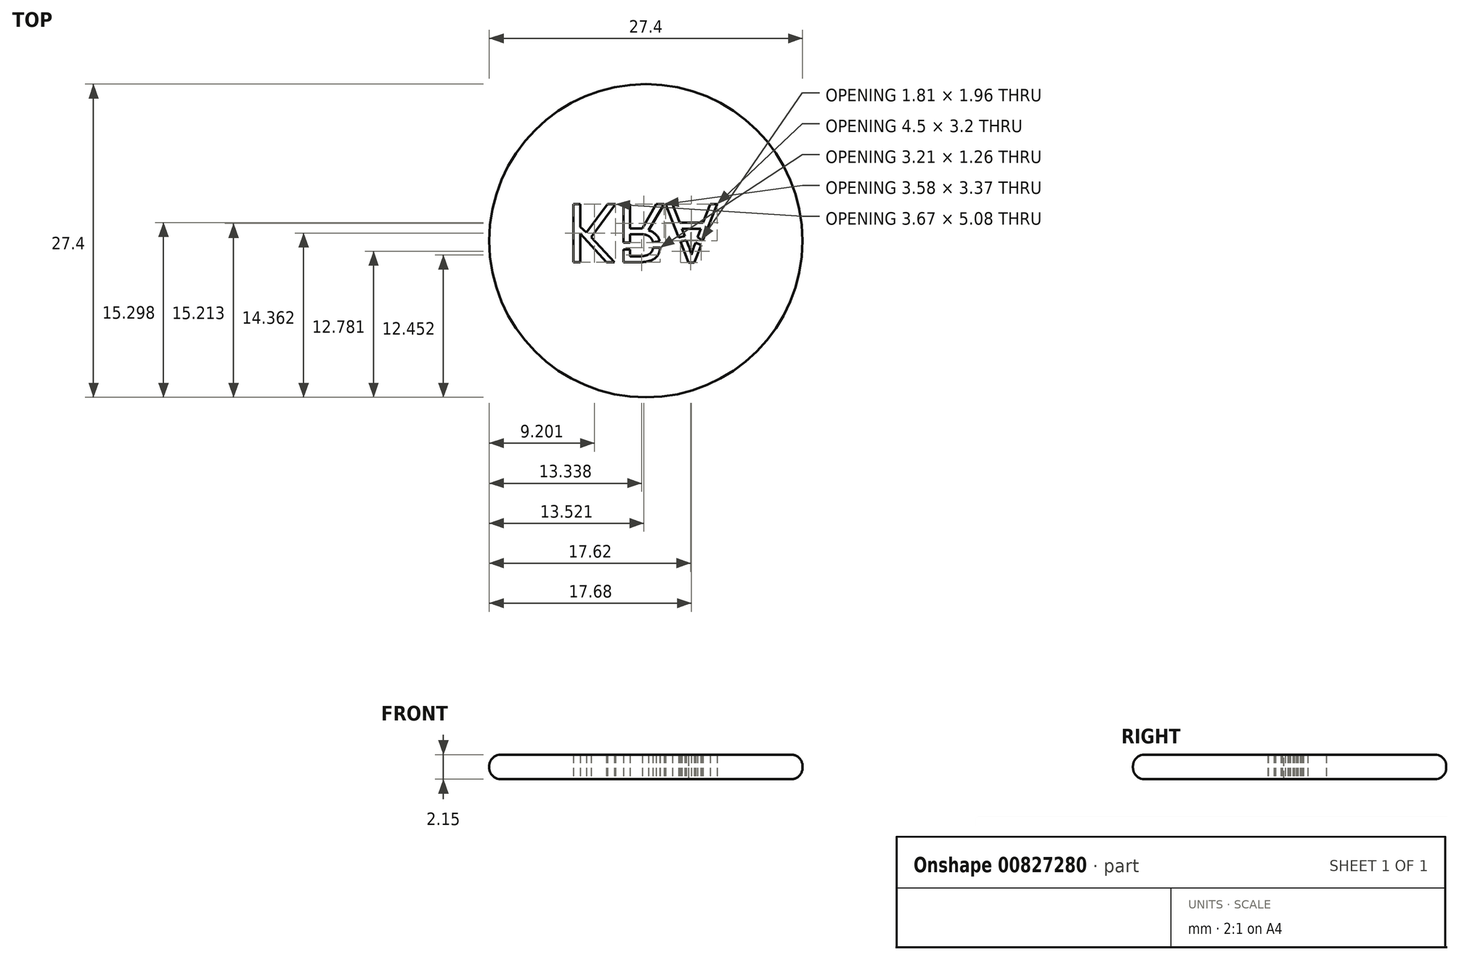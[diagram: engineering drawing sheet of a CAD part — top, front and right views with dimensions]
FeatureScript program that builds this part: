
annotation { "Feature Type Name" : "Feature", "Feature Type Description" : "" }
export const myFeature = defineFeature(function(context is Context, id is Id, definition is map)
    precondition{}
    {
        {
            var Q0;
            Q0=qCreatedBy(makeId("Top.planeOp"),FACE);
            var sketch = newSketch(context, id + "F0", { "sketchPlane" : qUnion([Q0])});
            skCircle(sketch, "E0", {"center": v(0, 0) * mm, "radius": 13.7 * mm});
            skSolve(sketch);
        }
        {
            var Q0;
            Q0=makeQuery(id+"F0.imprint","IMPRINT",FACE,{"disambiguationData":[TD([[makeQuery(id+"F0.imprint","IMPRINT",EDGE,{"derivedFrom":sQuery(id+"F0.wireOp",EDGE,"E0")}),1.0]])]});
            extrude(context, id + "F1", {"entities" : qUnion([Q0]), "depth" : 2.15 * mm, "offsetDistance" : 25 * mm});
        }
        {
            var Q0;
            Q0=makeQuery(id+"F1.opExtrude","CAP_FACE",FACE,{"disambiguationData":[OSD([sQuery(id+"F0.wireOp",EDGE,"E0")])],"isStart":false});
            var Q1;
            Q1=makeQuery(id+"F1.opExtrude","CAP_EDGE",EDGE,{"disambiguationData":[OSD([sQuery(id+"F0.wireOp",EDGE,"E0")])],"isStart":true});
            fillet(context, id + "F2", {"entities" : qUnion([Q0, Q1]), "radius" : 1 * mm, "tangentPropagation" : true, "allowEdgeOverflow" : false});
        }
        {
            var Q0;
            Q0=makeQuery(id+"F1.opExtrude","CAP_FACE",FACE,{"disambiguationData":[OSD([sQuery(id+"F0.wireOp",EDGE,"E0")])],"isStart":true});
            var sketch = newSketch(context, id + "F3", { "sketchPlane" : qUnion([Q0])});
            skText(sketch, "E1", { "text": "KRA", "fontName": "OpenSans-Regular.ttf"});
            skLineSegment(sketch, "E2", {"start": v(0.48, 0.62) * mm, "end": v(1.55, 0.62) * mm});
            skLineSegment(sketch, "E3", {"start": v(1.55, 0.58) * mm, "end": v(1.55, 0) * mm});
            skLineSegment(sketch, "E4", {"start": v(1.55, 0) * mm, "end": v(0.35, 0.17) * mm});
            skLineSegment(sketch, "E5", {"start": v(0.35, 0.17) * mm, "end": v(-2.35, 0.17) * mm});
            skLineSegment(sketch, "E6", {"start": v(-2.35, 0.17) * mm, "end": v(-2.35, 0.75) * mm});
            skLineSegment(sketch, "E7", {"start": v(-2.35, 0.75) * mm, "end": v(-0.85, 0.75) * mm});
            skLineSegment(sketch, "E8", {"start": v(2.6, 0.17) * mm, "end": v(3.94, -0.16) * mm});
            skLineSegment(sketch, "E9", {"start": v(2.29, -0.14) * mm, "end": v(3.86, -0.5) * mm});
            skLineSegment(sketch, "E10", {"start": v(5.16, 0.56) * mm, "end": v(4.03, 0) * mm});
            skLineSegment(sketch, "E11", {"start": v(5.23, 0.17) * mm, "end": v(4.21, -0.5) * mm});
            const initialGuessF3  = {"E1": [-0.00703, -0.0032, 1, 0, 0.00512]};
            skSetInitialGuess(sketch, initialGuessF3);
            skSolve(sketch);
        }
        {
            var Q0;
            Q0=makeQuery(id+"F3.imprint","IMPRINT",FACE,{"disambiguationData":[TD([[makeQuery(id+"F3.imprint","IMPRINT",EDGE,{"derivedFrom":sQuery(id+"F3.wireOp",EDGE,"E1.sketch_text.stroke-0")}),-1.0]])]});
            var Q1;
            Q1=makeQuery(id+"F3.imprint","IMPRINT",FACE,{"disambiguationData":[TD([[makeQuery(id+"F3.imprint","IMPRINT",EDGE,{"derivedFrom":sQuery(id+"F3.wireOp",EDGE,"E1.sketch_text.stroke-12")}),-1.0]])]});
            var Q2;
            {var subQ4=sQuery(id+"F3.wireOp",EDGE,"E1.sketch_text.stroke-15");Q2=makeQuery(id+"F3.imprint","IMPRINT",FACE,{"disambiguationData":[TD([[makeQuery(id+"F3.imprint","IMPRINT",EDGE,{"derivedFrom":subQ4}),-1.0]])]});}
            var Q3;
            {var subQ5=sQuery(id+"F3.wireOp",EDGE,"E1.sketch_text.stroke-35");Q3=makeQuery(id+"F3.imprint","IMPRINT",FACE,{"disambiguationData":[TD([[makeQuery(id+"F3.imprint","IMPRINT",EDGE,{"derivedFrom":subQ5}),-1.0]])]});}
            var Q4;
            Q4=makeQuery(id+"F3.imprint","IMPRINT",FACE,{"disambiguationData":[TD([[makeQuery(id+"F3.imprint","IMPRINT",EDGE,{"derivedFrom":sQuery(id+"F3.wireOp",EDGE,"E1.sketch_text.stroke-30")}),-1.0]])]});
            var Q5;
            Q5=makeQuery(id+"F1.opExtrude","CAP_FACE",FACE,{"disambiguationData":[OSD([sQuery(id+"F0.wireOp",EDGE,"E0")])],"isStart":false});
            extrude(context, id + "F4", {"entities" : qUnion([Q0, Q1, Q2, Q3, Q4]), "operationType" : NewBodyOperationType.REMOVE, "endBound" : BoundingType.UP_TO_SURFACE, "oppositeDirection" : true, "depth" : 25 * mm, "endBoundEntityFace" : qUnion([Q5]), "offsetDistance" : 25 * mm});
        }
    });
